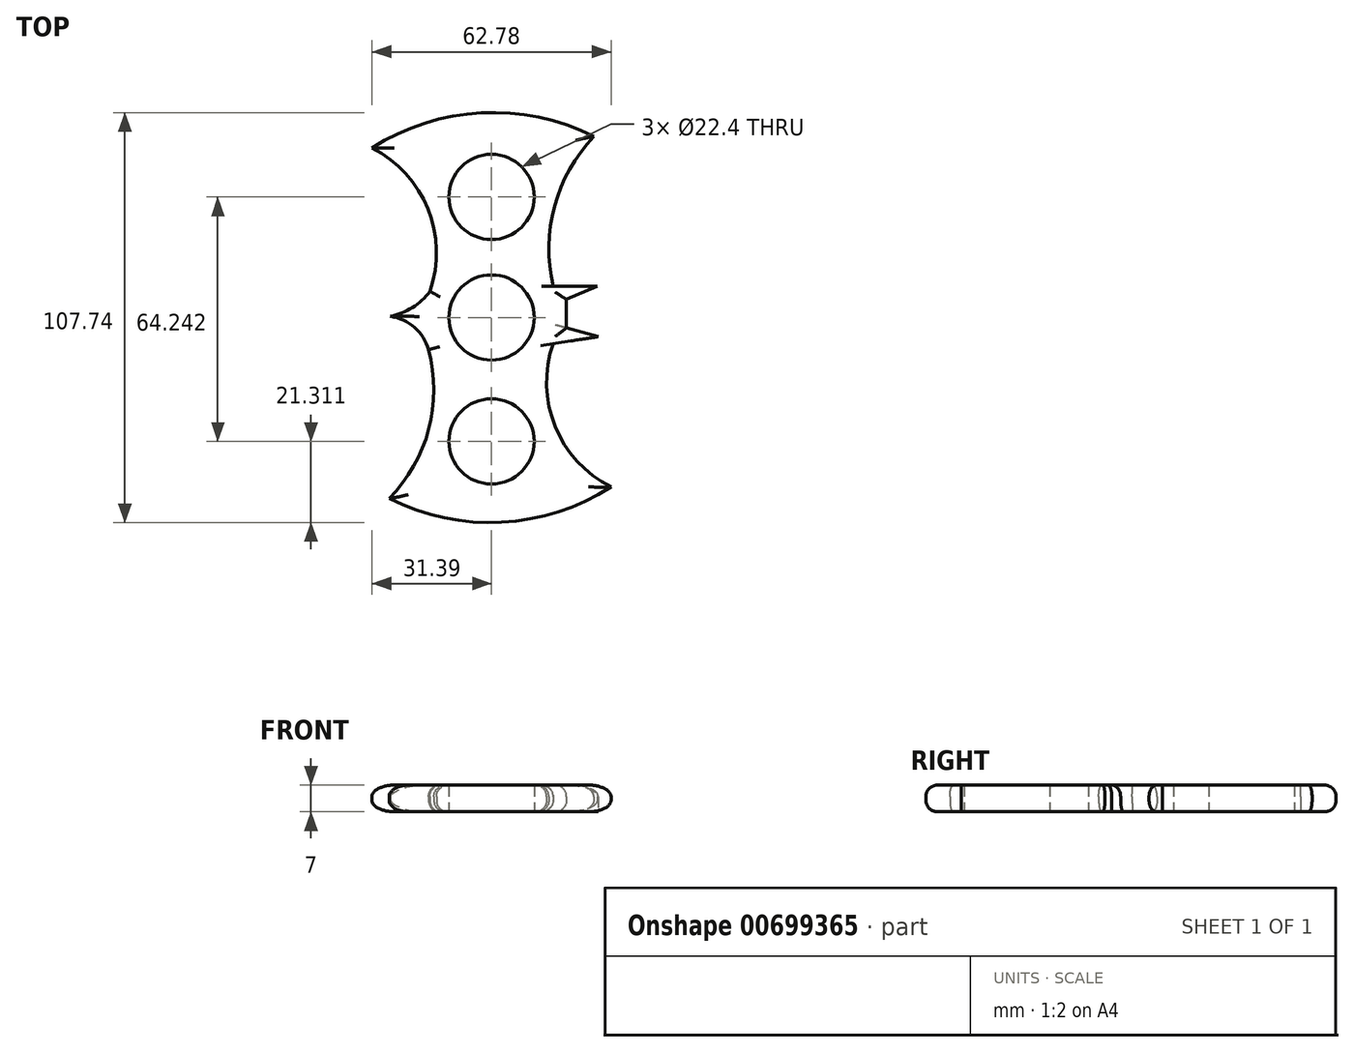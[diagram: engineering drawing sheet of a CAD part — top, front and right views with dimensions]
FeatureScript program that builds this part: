
annotation { "Feature Type Name" : "Feature", "Feature Type Description" : "" }
export const myFeature = defineFeature(function(context is Context, id is Id, definition is map)
    precondition{}
    {
        {
            var Q0;
            Q0=qCreatedBy(makeId("Top.planeOp"),FACE);
            var sketch = newSketch(context, id + "F0", { "sketchPlane" : qUnion([Q0])});
            skCircle(sketch, "E0", {"center": v(0, 0) * mm, "radius": 11.2 * mm});
            skCircle(sketch, "E1", {"center": v(0, 31.68) * mm, "radius": 11.2 * mm});
            skCircle(sketch, "E2.1.1", {"center": v(0, -32.56) * mm, "radius": 11.2 * mm});
            skPoint(sketch, "E2.center", {"position": v(0, -0.44) * mm});
            skArc(sketch, "E3", {"start": v(26.87, 47.57) * mm, "mid": v(-2.66, 53.8) * mm, "end": v(-31.4, 44.53) * mm});
            skArc(sketch, "E4", {"start": v(-16.2, 6.86) * mm, "mid": v(-16.7, 28.56) * mm, "end": v(-31.4, 44.53) * mm});
            skArc(sketch, "E5", {"start": v(-31.4, 0) * mm, "mid": v(-22.92, 1.48) * mm, "end": v(-16.2, 6.86) * mm});
            skArc(sketch, "E6.1.0", {"start": v(-26.87, -47.57) * mm, "mid": v(2.66, -53.8) * mm, "end": v(31.4, -44.53) * mm});
            skArc(sketch, "E6.1.1", {"start": v(16.2, -6.86) * mm, "mid": v(16.7, -28.56) * mm, "end": v(31.4, -44.53) * mm});
            skArc(sketch, "E7", {"start": v(-26.87, -47.57) * mm, "mid": v(-16.5, -29.4) * mm, "end": v(-16.53, -8.48) * mm});
            skArc(sketch, "E8", {"start": v(-16.53, -8.48) * mm, "mid": v(-22.22, -1.2) * mm, "end": v(-31.4, 0) * mm});
            skArc(sketch, "E9", {"start": v(26.87, 47.57) * mm, "mid": v(16.54, 29.23) * mm, "end": v(16.2, 8.2) * mm});
            skLineSegment(sketch, "E10", {"start": v(16.2, 8.2) * mm, "end": v(27.73, 8.2) * mm});
            skLineSegment(sketch, "E11", {"start": v(27.73, 8.2) * mm, "end": v(19.69, 4.74) * mm});
            skLineSegment(sketch, "E12", {"start": v(19.69, 4.74) * mm, "end": v(19.69, -2.73) * mm});
            skLineSegment(sketch, "E13", {"start": v(19.69, -2.73) * mm, "end": v(28.02, -5.03) * mm});
            skLineSegment(sketch, "E14", {"start": v(28.02, -5.03) * mm, "end": v(16.2, -6.86) * mm});
            skSolve(sketch);
        }
        {
            var Q0;
            Q0=makeQuery(id+"F0.imprint","IMPRINT",FACE,{"disambiguationData":[TD([[makeQuery(id+"F0.imprint","IMPRINT",EDGE,{"derivedFrom":sQuery(id+"F0.wireOp",EDGE,"E0")}),-1.0]])]});
            extrude(context, id + "F1", {"entities" : qUnion([Q0]), "depth" : 7 * mm, "offsetDistance" : 25 * mm});
        }
        {
            var Q0;
            Q0=makeQuery(id+"F1.opExtrude","CAP_EDGE",EDGE,{"disambiguationData":[OSD([sQuery(id+"F0.wireOp",EDGE,"E3")])],"isStart":false});
            var Q1;
            Q1=makeQuery(id+"F1.opExtrude","CAP_EDGE",EDGE,{"disambiguationData":[OSD([sQuery(id+"F0.wireOp",EDGE,"E6.1.0")])],"isStart":false});
            var Q2;
            Q2=makeQuery(id+"F1.opExtrude","CAP_EDGE",EDGE,{"disambiguationData":[OSD([sQuery(id+"F0.wireOp",EDGE,"E9")])],"isStart":false});
            var Q3;
            Q3=makeQuery(id+"F1.opExtrude","CAP_EDGE",EDGE,{"disambiguationData":[OSD([sQuery(id+"F0.wireOp",EDGE,"E4")])],"isStart":false});
            var Q4;
            Q4=makeQuery(id+"F1.opExtrude","CAP_EDGE",EDGE,{"disambiguationData":[OSD([sQuery(id+"F0.wireOp",EDGE,"E5")])],"isStart":false});
            var Q5;
            Q5=makeQuery(id+"F1.opExtrude","CAP_EDGE",EDGE,{"disambiguationData":[OSD([sQuery(id+"F0.wireOp",EDGE,"E7")])],"isStart":false});
            var Q6;
            Q6=makeQuery(id+"F1.opExtrude","CAP_EDGE",EDGE,{"disambiguationData":[OSD([sQuery(id+"F0.wireOp",EDGE,"E8")])],"isStart":false});
            var Q7;
            Q7=makeQuery(id+"F1.opExtrude","CAP_EDGE",EDGE,{"disambiguationData":[OSD([sQuery(id+"F0.wireOp",EDGE,"E6.1.1")])],"isStart":false});
            var Q8;
            Q8=makeQuery(id+"F1.opExtrude","CAP_EDGE",EDGE,{"disambiguationData":[OSD([sQuery(id+"F0.wireOp",EDGE,"E11")])],"isStart":false});
            var Q9;
            Q9=makeQuery(id+"F1.opExtrude","CAP_EDGE",EDGE,{"disambiguationData":[OSD([sQuery(id+"F0.wireOp",EDGE,"E12")])],"isStart":false});
            var Q10;
            Q10=makeQuery(id+"F1.opExtrude","CAP_EDGE",EDGE,{"disambiguationData":[OSD([sQuery(id+"F0.wireOp",EDGE,"E13")])],"isStart":false});
            var Q11;
            Q11=makeQuery(id+"F1.opExtrude","CAP_EDGE",EDGE,{"disambiguationData":[OSD([sQuery(id+"F0.wireOp",EDGE,"E7")])],"isStart":true});
            var Q12;
            Q12=makeQuery(id+"F1.opExtrude","CAP_EDGE",EDGE,{"disambiguationData":[OSD([sQuery(id+"F0.wireOp",EDGE,"E6.1.0")])],"isStart":true});
            var Q13;
            Q13=makeQuery(id+"F1.opExtrude","CAP_EDGE",EDGE,{"disambiguationData":[OSD([sQuery(id+"F0.wireOp",EDGE,"E6.1.1")])],"isStart":true});
            var Q14;
            Q14=makeQuery(id+"F1.opExtrude","CAP_EDGE",EDGE,{"disambiguationData":[OSD([sQuery(id+"F0.wireOp",EDGE,"E12")])],"isStart":true});
            var Q15;
            Q15=makeQuery(id+"F1.opExtrude","CAP_EDGE",EDGE,{"disambiguationData":[OSD([sQuery(id+"F0.wireOp",EDGE,"E9")])],"isStart":true});
            var Q16;
            Q16=makeQuery(id+"F1.opExtrude","CAP_EDGE",EDGE,{"disambiguationData":[OSD([sQuery(id+"F0.wireOp",EDGE,"E11")])],"isStart":true});
            var Q17;
            Q17=makeQuery(id+"F1.opExtrude","CAP_EDGE",EDGE,{"disambiguationData":[OSD([sQuery(id+"F0.wireOp",EDGE,"E3")])],"isStart":true});
            var Q18;
            Q18=makeQuery(id+"F1.opExtrude","CAP_EDGE",EDGE,{"disambiguationData":[OSD([sQuery(id+"F0.wireOp",EDGE,"E4")])],"isStart":true});
            var Q19;
            Q19=makeQuery(id+"F1.opExtrude","CAP_EDGE",EDGE,{"disambiguationData":[OSD([sQuery(id+"F0.wireOp",EDGE,"E5")])],"isStart":true});
            fillet(context, id + "F2", {"entities" : qUnion([Q0, Q1, Q2, Q3, Q4, Q5, Q6, Q7, Q8, Q9, Q10, Q11, Q12, Q13, Q14, Q15, Q16, Q17, Q18, Q19]), "radius" : 3 * mm, "tangentPropagation" : true, "allowEdgeOverflow" : false});
        }
    });
